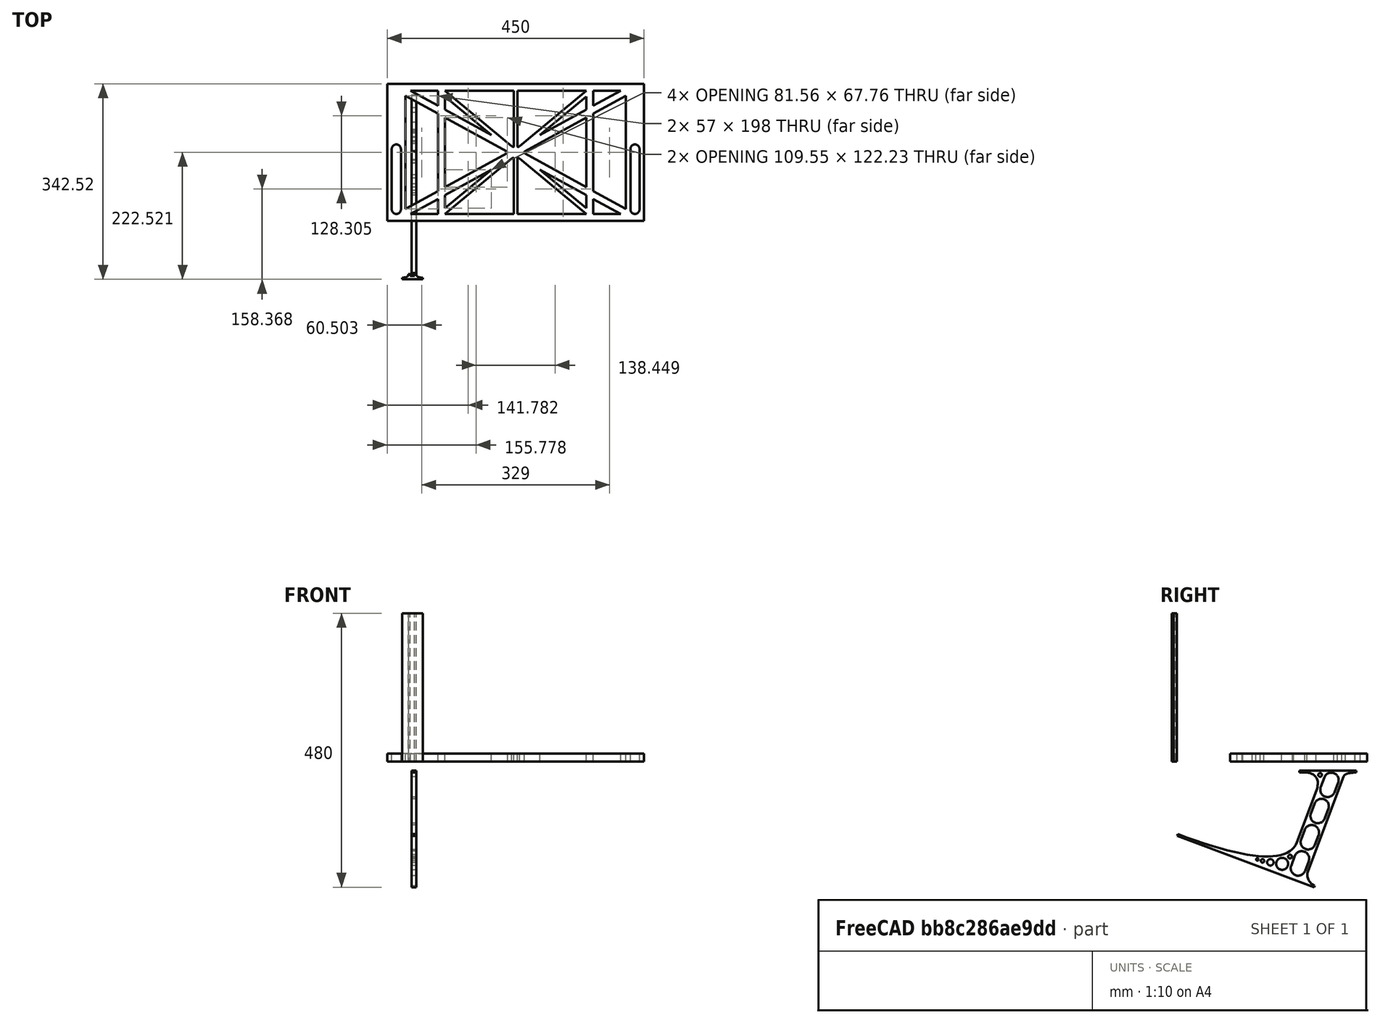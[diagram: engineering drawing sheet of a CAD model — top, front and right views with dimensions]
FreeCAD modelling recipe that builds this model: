
FCSTD DOCUMENT  (FreeCAD 0.19R0.19.2)
Label: laptopStand064
License: All rights reserved
LicenseURL: http://en.wikipedia.org/wiki/All_rights_reserved
objects: Sketcher::SketchObject×3, Part::Extrusion×3
note: 6 computed .brp shape members not serialized (recipe doc carries the construction recipe); baked Part::Feature solids carry a one-line shape summary decoded from their .brp

FEATURE [Sketcher::SketchObject] Sketch
  FullyConstrained = false
  sketch-geometry (101):
    g0: LineSegment StartX=-10.9272 StartY=-82.7794 StartZ=0 EndX=46.0728 EndY=-51.4823 EndZ=0
    g1: LineSegment StartX=366.073 StartY=-91.7794 StartZ=0 EndX=318.073 EndY=-65.424 EndZ=0
    g2: LineSegment StartX=-10.9272 StartY=77.3346 StartZ=0 EndX=-10.9272 EndY=-82.7794 EndZ=0
    g3: LineSegment StartX=375.073 StartY=-82.7794 StartZ=0 EndX=375.073 EndY=83.9235 EndZ=0
    g4: LineSegment StartX=-1.92719 StartY=-91.7794 StartZ=0 EndX=46.0728 EndY=-91.7794 EndZ=0
    g5: LineSegment StartX=318.073 StartY=124.221 StartZ=0 EndX=366.073 EndY=124.221 EndZ=0
    g6: LineSegment StartX=306.073 StartY=-81.8102 StartZ=0 EndX=224.513 EndY=-14.0532 EndZ=0
    g7: LineSegment StartX=58.0728 StartY=114.251 StartZ=0 EndX=139.632 EndY=46.4944 EndZ=0
    g8: LineSegment StartX=306.073 StartY=124.221 StartZ=0 EndX=189.124 EndY=27.0628 EndZ=0
    g9: LineSegment StartX=58.0728 StartY=-91.7794 StartZ=0 EndX=175.022 EndY=5.37834 EndZ=0
    g10: LineSegment StartX=58.0728 StartY=-81.8102 StartZ=0 EndX=58.0728 EndY=-58.8351 EndZ=0
    g11: LineSegment StartX=306.073 StartY=114.251 StartZ=0 EndX=306.073 EndY=91.2763 EndZ=0
    g12: LineSegment StartX=224.513 StartY=46.4944 StartZ=0 EndX=306.073 EndY=114.251 EndZ=0
    g13: LineSegment StartX=175.022 StartY=27.0628 StartZ=0 EndX=58.0728 EndY=124.221 EndZ=0
    g14: LineSegment StartX=139.632 StartY=-14.0532 StartZ=0 EndX=58.0728 EndY=-81.8102 EndZ=0
    g15: LineSegment StartX=224.513 StartY=46.4944 StartZ=0 EndX=306.073 EndY=91.2763 EndZ=0
    g16: LineSegment StartX=139.632 StartY=-14.0532 StartZ=0 EndX=58.0728 EndY=-58.8351 EndZ=0
    g17: LineSegment StartX=189.124 StartY=5.37834 StartZ=0 EndX=306.073 EndY=-91.7794 EndZ=0
    g18: LineSegment StartX=306.073 StartY=77.3346 StartZ=0 EndX=306.073 EndY=-44.8935 EndZ=0
    g19: LineSegment StartX=318.073 StartY=83.9235 StartZ=0 EndX=318.073 EndY=-51.4823 EndZ=0
    g20: LineSegment StartX=306.073 StartY=-58.8351 StartZ=0 EndX=224.513 EndY=-14.0532 EndZ=0
    g21: LineSegment StartX=306.073 StartY=-58.8351 StartZ=0 EndX=306.073 EndY=-81.8102 EndZ=0
    g22: LineSegment StartX=318.073 StartY=-51.4823 StartZ=0 EndX=375.073 EndY=-82.7794 EndZ=0
    g23: LineSegment StartX=318.073 StartY=-65.424 StartZ=0 EndX=318.073 EndY=-91.7794 EndZ=0
    g24: LineSegment StartX=318.073 StartY=-91.7794 StartZ=0 EndX=366.073 EndY=-91.7794 EndZ=0
    g25: LineSegment StartX=58.0728 StartY=-44.8935 StartZ=0 EndX=58.0728 EndY=77.3346 EndZ=0
    g26: LineSegment StartX=46.0728 StartY=-65.424 StartZ=0 EndX=-1.92719 EndY=-91.7794 EndZ=0
    g27: LineSegment StartX=46.0728 StartY=-65.424 StartZ=0 EndX=46.0728 EndY=-91.7794 EndZ=0
    g28: LineSegment StartX=58.0728 StartY=91.2763 StartZ=0 EndX=58.0728 EndY=114.251 EndZ=0
    g29: LineSegment StartX=46.0728 StartY=77.3346 StartZ=0 EndX=46.0728 EndY=-51.4823 EndZ=0
    g30: LineSegment StartX=58.0728 StartY=91.2763 StartZ=0 EndX=139.632 EndY=46.4944 EndZ=0
    g31: LineSegment StartX=-42.9272 StartY=136.221 StartZ=0 EndX=-42.9272 EndY=-103.779 EndZ=0
    g32: LineSegment StartX=407.073 StartY=136.221 StartZ=0 EndX=407.073 EndY=-103.779 EndZ=0
    g33: LineSegment StartX=179.022 StartY=27.0628 StartZ=0 EndX=179.022 EndY=124.221 EndZ=0
    g34: LineSegment StartX=185.124 StartY=27.0628 StartZ=0 EndX=185.124 EndY=124.221 EndZ=0
    g35: ArcOfCircle CenterX=-26.9272 CenterY=22.1087 CenterZ=0 NormalX=0 NormalY=0 NormalZ=1 AngleXU=0 Radius=8 StartAngle=1e-16 EndAngle=3.14159
    g36: ArcOfCircle CenterX=-26.9272 CenterY=-83.7794 CenterZ=0 NormalX=0 NormalY=0 NormalZ=1 AngleXU=0 Radius=8 StartAngle=3.14159 EndAngle=6.28319
    g37: LineSegment StartX=-34.9272 StartY=22.1087 StartZ=0 EndX=-34.9272 EndY=-83.7794 EndZ=0
    g38: LineSegment StartX=-18.9272 StartY=22.1087 StartZ=0 EndX=-18.9272 EndY=-83.7794 EndZ=0
    g39: LineSegment StartX=185.124 StartY=-91.7794 StartZ=0 EndX=306.073 EndY=-91.7794 EndZ=0
    g40: LineSegment StartX=179.022 StartY=-91.7794 StartZ=0 EndX=58.0728 EndY=-91.7794 EndZ=0
    g41: LineSegment StartX=306.073 StartY=124.221 StartZ=0 EndX=185.124 EndY=124.221 EndZ=0
    g42: LineSegment StartX=179.022 StartY=124.221 StartZ=0 EndX=58.0728 EndY=124.221 EndZ=0
    g43: ArcOfCircle CenterX=391.073 CenterY=22.1087 CenterZ=0 NormalX=0 NormalY=0 NormalZ=1 AngleXU=0 Radius=8 StartAngle=-4.4e-15 EndAngle=3.14159
    g44: LineSegment StartX=399.073 StartY=22.1087 StartZ=0 EndX=399.073 EndY=-83.7794 EndZ=0
    g45: LineSegment StartX=383.073 StartY=22.1087 StartZ=0 EndX=383.073 EndY=-83.7794 EndZ=0
    g46: ArcOfCircle CenterX=391.073 CenterY=-83.7794 CenterZ=0 NormalX=0 NormalY=0 NormalZ=1 AngleXU=0 Radius=8 StartAngle=3.14159 EndAngle=6.28319
    g47: Circle CenterX=175.022 CenterY=27.0628 CenterZ=0 NormalX=0 NormalY=0 NormalZ=1 AngleXU=0 Radius=1
    g48: Circle CenterX=179.022 CenterY=24.8665 CenterZ=0 NormalX=0 NormalY=0 NormalZ=1 AngleXU=0 Radius=1
    g49: Circle CenterX=179.022 CenterY=27.0628 CenterZ=0 NormalX=0 NormalY=0 NormalZ=1 AngleXU=0 Radius=1
    g50: BSplineCurve PolesCount=3 KnotsCount=2 Degree=2 IsPeriodic=0
    g51: GeomPoint X=175.022 Y=27.0628 Z=0
    g52: GeomPoint X=179.022 Y=27.0628 Z=0
    g53: Circle CenterX=189.124 CenterY=27.0628 CenterZ=0 NormalX=0 NormalY=0 NormalZ=1 AngleXU=0 Radius=1
    g54: Circle CenterX=185.124 CenterY=24.8665 CenterZ=0 NormalX=0 NormalY=0 NormalZ=1 AngleXU=0 Radius=1
    g55: Circle CenterX=185.124 CenterY=27.0628 CenterZ=0 NormalX=0 NormalY=0 NormalZ=1 AngleXU=0 Radius=1
    g56: BSplineCurve PolesCount=3 KnotsCount=2 Degree=2 IsPeriodic=0
    g57: GeomPoint X=189.124 Y=27.0628 Z=0
    g58: GeomPoint X=185.124 Y=27.0628 Z=0
    g59: Circle CenterX=175.022 CenterY=5.37834 CenterZ=0 NormalX=0 NormalY=0 NormalZ=1 AngleXU=0 Radius=1
    g60: Circle CenterX=179.022 CenterY=7.57463 CenterZ=0 NormalX=0 NormalY=0 NormalZ=1 AngleXU=0 Radius=1
    g61: Circle CenterX=179.022 CenterY=5.34704 CenterZ=0 NormalX=0 NormalY=0 NormalZ=1 AngleXU=0 Radius=1
    g62: BSplineCurve PolesCount=3 KnotsCount=2 Degree=2 IsPeriodic=0
    g63: GeomPoint X=175.022 Y=5.37834 Z=0
    g64: GeomPoint X=179.022 Y=5.34704 Z=0
    g65: Circle CenterX=189.124 CenterY=5.37834 CenterZ=0 NormalX=0 NormalY=0 NormalZ=1 AngleXU=0 Radius=1
    g66: Circle CenterX=185.124 CenterY=7.57463 CenterZ=0 NormalX=0 NormalY=0 NormalZ=1 AngleXU=0 Radius=1
    g67: Circle CenterX=185.124 CenterY=5.34704 CenterZ=0 NormalX=0 NormalY=0 NormalZ=1 AngleXU=0 Radius=1
    g68: BSplineCurve PolesCount=3 KnotsCount=2 Degree=2 IsPeriodic=0
    g69: GeomPoint X=189.124 Y=5.37834 Z=0
    g70: GeomPoint X=185.124 Y=5.34704 Z=0
    g71: LineSegment StartX=179.022 StartY=5.34704 StartZ=0 EndX=179.022 EndY=-91.7794 EndZ=0
    g72: LineSegment StartX=185.124 StartY=-91.7794 StartZ=0 EndX=185.124 EndY=5.34704 EndZ=0
    g73: Circle CenterX=165.871 CenterY=18.1458 CenterZ=0 NormalX=0 NormalY=0 NormalZ=1 AngleXU=0 Radius=1
    g74: Circle CenterX=169.377 CenterY=16.2206 CenterZ=0 NormalX=0 NormalY=0 NormalZ=1 AngleXU=0 Radius=1
    g75: Circle CenterX=165.871 CenterY=14.2954 CenterZ=0 NormalX=0 NormalY=0 NormalZ=1 AngleXU=0 Radius=1
    g76: BSplineCurve PolesCount=3 KnotsCount=2 Degree=2 IsPeriodic=0
    g77: GeomPoint X=165.871 Y=18.1458 Z=0
    g78: GeomPoint X=165.871 Y=14.2954 Z=0
    g79: Circle CenterX=198.275 CenterY=18.1458 CenterZ=0 NormalX=0 NormalY=0 NormalZ=1 AngleXU=0 Radius=1
    g80: Circle CenterX=194.768 CenterY=16.2206 CenterZ=0 NormalX=0 NormalY=0 NormalZ=1 AngleXU=0 Radius=1
    g81: Circle CenterX=198.275 CenterY=14.2954 CenterZ=0 NormalX=0 NormalY=0 NormalZ=1 AngleXU=0 Radius=1
    g82: BSplineCurve PolesCount=3 KnotsCount=2 Degree=2 IsPeriodic=0
    g83: GeomPoint X=198.275 Y=18.1458 Z=0
    g84: GeomPoint X=198.275 Y=14.2954 Z=0
    g85: LineSegment StartX=165.871 StartY=18.1458 StartZ=0 EndX=58.0728 EndY=77.3346 EndZ=0
    g86: LineSegment StartX=58.0728 StartY=-44.8935 StartZ=0 EndX=165.871 EndY=14.2954 EndZ=0
    g87: LineSegment StartX=198.275 StartY=18.1458 StartZ=0 EndX=306.073 EndY=77.3346 EndZ=0
    g88: LineSegment StartX=198.275 StartY=14.2954 StartZ=0 EndX=306.073 EndY=-44.8935 EndZ=0
    g89: LineSegment StartX=407.073 StartY=-103.779 StartZ=0 EndX=-42.9272 EndY=-103.779 EndZ=0
    g90: LineSegment StartX=407.073 StartY=136.221 StartZ=0 EndX=-42.9272 EndY=136.221 EndZ=0
    g91: LineSegment StartX=-26.9272 StartY=136.221 StartZ=0 EndX=-26.9272 EndY=98.2206 EndZ=0
    g92: LineSegment StartX=46.0728 StartY=77.3346 StartZ=0 EndX=-10.9272 EndY=77.3346 EndZ=0
    g93: LineSegment StartX=46.0728 StartY=105.865 StartZ=0 EndX=31.5028 EndY=105.865 EndZ=0
    g94: LineSegment StartX=46.0728 StartY=124.221 StartZ=0 EndX=46.0728 EndY=105.865 EndZ=0
    g95: LineSegment StartX=-1.92719 StartY=124.221 StartZ=0 EndX=31.5028 EndY=105.865 EndZ=0
    g96: LineSegment StartX=46.0728 StartY=124.221 StartZ=0 EndX=-1.92719 EndY=124.221 EndZ=0
    g97: LineSegment StartX=318.073 StartY=83.9235 StartZ=0 EndX=375.073 EndY=83.9235 EndZ=0
    g98: LineSegment StartX=318.073 StartY=105.865 StartZ=0 EndX=332.643 EndY=105.865 EndZ=0
    g99: LineSegment StartX=332.643 StartY=105.865 StartZ=0 EndX=366.073 EndY=124.221 EndZ=0
    g100: LineSegment StartX=318.073 StartY=124.221 StartZ=0 EndX=318.073 EndY=105.865 EndZ=0
  constraints (192):
    c: Horizontal(g4)
    c: Horizontal(g5)
    c: Coincident(g30,g7)
    c: Coincident(g12,g15)
    c: Coincident(g16,g14)
    c: Coincident(g20,g6)
    c: Coincident(g12,g11)
    c: Tangent(g11,g18)
    c: Coincident(g15,g11)
    c: Coincident(g21,g6)
    c: Tangent(g1,g20)
    c: Tangent(g18,g21)
    c: Coincident(g19,g22)
    c: Coincident(g23,g1)
    c: Tangent(g19,g23)
    c: Coincident(g14,g10)
    c: Tangent(g10,g25)
    c: Coincident(g16,g10)
    c: Tangent(g16,g26)
    c: Coincident(g27,g26)
    c: Coincident(g0,g29)
    c: Tangent(g25,g28)
    c: Coincident(g7,g28)
    c: Coincident(g30,g28)
    c: Block(g13)
    c: Block(g8)
    c: Block(g22)
    c: Block(g3)
    c: Block(g20)
    c: Block(g21)
    c: Block(g1)
    c: Block(g23)
    c: Block(g12)
    c: Block(g17)
    c: Block(g9)
    c: Block(g16)
    c: Block(g14)
    c: Block(g27)
    c: Block(g26)
    c: Block(g0)
    c: Block(g2)
    c: Block(g7)
    c: Block(g28)
    c: Block(g18)
    c: Block(g5)
    c: Block(g24)
    c: Block(g4)
    c: Vertical(g31)
    c: Vertical(g32)
    c: Block(g32)
    c: Block(g31)
    c: Vertical(g33)
    c: Vertical(g34)
    c: Block(g33)
    c: Block(g34)
    c: Tangent(g35,g38) = 1.5708
    c: Tangent(g35,g37) = -1.5708
    c: Tangent(g37,g36) = -1.5708
    c: Tangent(g38,g36) = 1.5708
    c: Vertical(g37)
    c: Equal(g35,g36)
    c: Block(g38)
    c: Block(g37)
    c: Coincident(g39,g17)
    c: Horizontal(g39)
    c: Coincident(g40,g9)
    c: Horizontal(g40)
    c: Coincident(g41,g8)
    c: Coincident(g41,g34)
    c: Horizontal(g41)
    c: Coincident(g42,g33)
    c: Coincident(g42,g13)
    c: Horizontal(g42)
    c: Tangent(g43,g44) = 1.5708
    c: Tangent(g44,g46) = 1.5708
    c: Equal(g43,g46)
    c: Coincident(g45,g43)
    c: Coincident(g45,g46)
    c: Block(g44)
    c: Block(g45)
    c: Coincident(g50,g13)
    c: Weight(g47) = 1
    c: Equal(g47,g48)
    c: Equal(g47,g49)
    c: Coincident(g50,g33)
    c: InternalAlignment(g47,g50)
    c: InternalAlignment(g48,g50)
    c: InternalAlignment(g49,g50)
    c: InternalAlignment(g51,g50)
    c: InternalAlignment(g52,g50)
    c: Coincident(g56,g8)
    c: Weight(g53) = 1
    c: Equal(g53,g54)
    c: Equal(g53,g55)
    c: Coincident(g56,g34)
    c: InternalAlignment(g53,g56)
    c: InternalAlignment(g54,g56)
    c: InternalAlignment(g55,g56)
    c: InternalAlignment(g57,g56)
    c: InternalAlignment(g58,g56)
    c: Block(g56)
    c: Block(g50)
    c: Coincident(g62,g9)
    c: Weight(g59) = 1
    c: Equal(g59,g60)
    c: Equal(g59,g61)
    c: InternalAlignment(g59,g62)
    c: InternalAlignment(g60,g62)
    c: InternalAlignment(g61,g62)
    c: InternalAlignment(g63,g62)
    c: InternalAlignment(g64,g62)
    c: Weight(g65) = 1
    c: Equal(g65,g66)
    c: Equal(g65,g67)
    c: InternalAlignment(g65,g68)
    c: InternalAlignment(g66,g68)
    c: InternalAlignment(g67,g68)
    c: InternalAlignment(g69,g68)
    c: InternalAlignment(g70,g68)
    c: Block(g68)
    c: Block(g62)
    c: Coincident(g71,g62)
    c: Coincident(g71,g40)
    c: Vertical(g71)
    c: Coincident(g72,g39)
    c: Coincident(g72,g68)
    c: Vertical(g72)
    c: Weight(g73) = 1
    c: Equal(g73,g74)
    c: Equal(g73,g75)
    c: InternalAlignment(g73,g76)
    c: InternalAlignment(g74,g76)
    c: InternalAlignment(g75,g76)
    c: InternalAlignment(g77,g76)
    c: InternalAlignment(g78,g76)
    c: Weight(g79) = 1
    c: Equal(g79,g80)
    c: Equal(g79,g81)
    c: InternalAlignment(g79,g82)
    c: InternalAlignment(g80,g82)
    c: InternalAlignment(g81,g82)
    c: InternalAlignment(g83,g82)
    c: InternalAlignment(g84,g82)
    c: Block(g76)
    c: Block(g82)
    c: Coincident(g85,g76)
    c: Coincident(g85,g25)
    c: Coincident(g86,g25)
    c: Coincident(g86,g76)
    c: Coincident(g87,g82)
    c: Coincident(g87,g18)
    c: Coincident(g88,g82)
    c: Coincident(g88,g18)
    c: Block(g25)
    c: Coincident(g89,g32)
    c: Coincident(g89,g31)
    c: Horizontal(g89)
    c: Distance(g89) = 450
    c: Coincident(g90,g32)
    c: Coincident(g90,g31)
    c: Horizontal(g90)
    c: PointOnObject(g91,g90)
    c: Vertical(g91)
    c: Distance(g91) = 38
    c: Horizontal(g92)
    c: Coincident(g29,g92)
    c: Horizontal(g93)
    c: Vertical(g94)
    c: Block(g94)
    c: Block(g93)
    c: Block(g92)
    c: Distance(g94) = 18.3554
    c: Coincident(g96,g94)
    c: Coincident(g96,g95)
    c: Horizontal(g96)
    c: Block(g96)
    c: Block(g95)
    c: Coincident(g93,g95)
    c: Coincident(g2,g92)
    c: Coincident(g97,g19)
    c: Horizontal(g97)
    c: Horizontal(g98)
    c: Block(g97)
    c: Block(g11)
    c: Coincident(g99,g5)
    c: Coincident(g100,g5)
    c: Coincident(g100,g98)
    c: Vertical(g100)
    c: Block(g100)
    c: Coincident(g98,g99)
    c: Block(g99)
    c: Coincident(g3,g97)
FEATURE [Sketcher::SketchObject] Sketch001
  FullyConstrained = true
  MapMode = 4
  Placement = pos=(0,0,0) rot=(0.57735,0.57735,0.57735;2.0944rad)
  Support = -> [Sketch]
  sketch-geometry (46):
    g0: BSplineCurve PolesCount=3 KnotsCount=2 Degree=2 IsPeriodic=0
    g1: ArcOfCircle CenterX=73.1223 CenterY=-32.291 CenterZ=0 NormalX=0 NormalY=0 NormalZ=1 AngleXU=0 Radius=13 StartAngle=5.92268 EndAngle=9.06428
    g2: ArcOfCircle CenterX=66.7816 CenterY=-49.1439 CenterZ=0 NormalX=0 NormalY=0 NormalZ=1 AngleXU=0 Radius=13 StartAngle=2.78068 EndAngle=5.92131
    g3: ArcOfCircle CenterX=55.9263 CenterY=-78.1807 CenterZ=0 NormalX=0 NormalY=0 NormalZ=1 AngleXU=0 Radius=13 StartAngle=5.92268 EndAngle=9.06428
    g4: ArcOfCircle CenterX=49.5884 CenterY=-95.0342 CenterZ=0 NormalX=0 NormalY=0 NormalZ=1 AngleXU=0 Radius=13 StartAngle=2.78068 EndAngle=5.92131
    g5: ArcOfCircle CenterX=38.7206 CenterY=-124.067 CenterZ=0 NormalX=0 NormalY=0 NormalZ=1 AngleXU=0 Radius=13 StartAngle=5.92268 EndAngle=9.06428
    g6: ArcOfCircle CenterX=32.3875 CenterY=-140.92 CenterZ=0 NormalX=0 NormalY=0 NormalZ=1 AngleXU=0 Radius=13 StartAngle=2.78068 EndAngle=5.92131
    g7: ArcOfCircle CenterX=21.4715 CenterY=-169.934 CenterZ=0 NormalX=0 NormalY=0 NormalZ=1 AngleXU=0 Radius=13 StartAngle=5.92268 EndAngle=9.06428
    g8: ArcOfCircle CenterX=15.1336 CenterY=-186.787 CenterZ=0 NormalX=0 NormalY=0 NormalZ=1 AngleXU=0 Radius=13 StartAngle=2.78068 EndAngle=5.92131
    g9-g12: Circle x4 (B-spline internal-alignment scaffolding for g13; pole/knot coordinates omitted)
    g13: BSplineCurve PolesCount=4 KnotsCount=2 Degree=3 IsPeriodic=0
    g14: GeomPoint X=28.8094 Y=-19.0875 Z=0
    g15: GeomPoint X=47.0443 Y=-50.4712 Z=0
    g16: Circle CenterX=53.5586 CenterY=-23.2695 CenterZ=0 NormalX=0 NormalY=0 NormalZ=1 AngleXU=0 Radius=3.24518
    g17: Circle CenterX=-195.441 CenterY=-127.082 CenterZ=0 NormalX=0 NormalY=0 NormalZ=1 AngleXU=0 Radius=1
    g18: Circle CenterX=-8.24091 CenterY=-197.481 CenterZ=0 NormalX=0 NormalY=0 NormalZ=1 AngleXU=0 Radius=1
    g19: Circle CenterX=12.8789 CenterY=-141.321 CenterZ=0 NormalX=0 NormalY=0 NormalZ=1 AngleXU=0 Radius=1
    g20: BSplineCurve PolesCount=3 KnotsCount=2 Degree=2 IsPeriodic=0
    g21: GeomPoint X=-195.441 Y=-127.082 Z=0
    g22: GeomPoint X=12.8789 Y=-141.321 Z=0
    g23: Circle CenterX=-12.8016 CenterY=-179.036 CenterZ=0 NormalX=0 NormalY=0 NormalZ=1 AngleXU=0 Radius=10.5072
    g24: Circle CenterX=0.933922 CenterY=-166.43 CenterZ=0 NormalX=0 NormalY=0 NormalZ=1 AngleXU=0 Radius=3.26661
    g25: Circle CenterX=-33.5518 CenterY=-176.44 CenterZ=0 NormalX=0 NormalY=0 NormalZ=1 AngleXU=0 Radius=5.64388
    g26: Circle CenterX=-47.2366 CenterY=-173.859 CenterZ=0 NormalX=0 NormalY=0 NormalZ=1 AngleXU=0 Radius=3.01653
    g27: Circle CenterX=-56.2595 CenterY=-171.456 CenterZ=0 NormalX=0 NormalY=0 NormalZ=1 AngleXU=0 Radius=2.12826
    g28: ArcOfCircle CenterX=51.2151 CenterY=-198.473 CenterZ=0 NormalX=0 NormalY=0 NormalZ=1 AngleXU=0 Radius=20 StartAngle=2.78189 EndAngle=4.35269
    g29: LineSegment StartX=32.4951 StartY=-191.433 StartZ=0 EndX=94.6578 EndY=-26.1352 EndZ=0
    g30: LineSegment StartX=43.1192 StartY=-220.001 StartZ=0 EndX=-196.497 EndY=-129.89 EndZ=0
    g31: LineSegment StartX=43.1192 StartY=-220.001 StartZ=0 EndX=44.1752 EndY=-217.193 EndZ=0
    g32: LineSegment StartX=117.223 StartY=-19.0875 StartZ=0 EndX=117.223 EndY=-16.0875 EndZ=0
    g33: LineSegment StartX=117.223 StartY=-16.0875 StartZ=0 EndX=17.2232 EndY=-16.0875 EndZ=0
    g34: LineSegment StartX=17.2232 StartY=-16.0875 StartZ=0 EndX=17.2232 EndY=-19.0875 EndZ=0
    g35: LineSegment StartX=28.8094 StartY=-19.0875 StartZ=0 EndX=17.2232 EndY=-19.0875 EndZ=0
    g36: LineSegment StartX=47.0443 StartY=-50.4712 StartZ=0 EndX=12.8789 EndY=-141.321 EndZ=0
    g37: LineSegment StartX=-195.441 StartY=-127.082 StartZ=0 EndX=-196.497 EndY=-129.89 EndZ=0
    g38: LineSegment StartX=85.2866 StartY=-36.8766 StartZ=0 EndX=78.9396 EndY=-53.7463 EndZ=0
    g39: LineSegment StartX=60.9579 StartY=-27.7053 StartZ=0 EndX=54.6191 EndY=-44.5532 EndZ=0
    g40: LineSegment StartX=68.0907 StartY=-82.7664 StartZ=0 EndX=61.7465 EndY=-99.6365 EndZ=0
    g41: LineSegment StartX=43.7619 StartY=-73.595 StartZ=0 EndX=37.426 EndY=-90.4435 EndZ=0
    g42: LineSegment StartX=50.885 StartY=-128.652 StartZ=0 EndX=44.5456 EndY=-145.522 EndZ=0
    g43: LineSegment StartX=26.5562 StartY=-119.481 StartZ=0 EndX=20.2251 EndY=-136.329 EndZ=0
    g44: LineSegment StartX=9.3071 StartY=-165.349 StartZ=0 EndX=2.97115 EndY=-182.197 EndZ=0
    g45: LineSegment StartX=33.6358 StartY=-174.52 StartZ=0 EndX=27.2917 EndY=-191.39 EndZ=0
  constraints (71):
    c: Block(g0)
    c: Block(g1)
    c: Block(g2)
    c: Block(g4)
    c: Block(g3)
    c: Block(g6)
    c: Block(g5)
    c: Block(g8)
    c: Block(g7)
    c: Weight(g9) = 1
    c: Equal(g9,g10)
    c: Equal(g9,g11)
    c: Equal(g9,g12)
    c: InternalAlignment(g9-g12 -> g13) x4
    c: InternalAlignment(g14,g13)
    c: InternalAlignment(g15,g13)
    c: Block(g16)
    c: Weight(g17) = 1
    c: Equal(g17,g18)
    c: Equal(g17,g19)
    c: InternalAlignment(g17,g20)
    c: InternalAlignment(g18,g20)
    c: InternalAlignment(g19,g20)
    c: InternalAlignment(g21,g20)
    c: InternalAlignment(g22,g20)
    c: Block(g20)
    c: Block(g23)
    c: Block(g24)
    c: Block(g25)
    c: Block(g26)
    c: Block(g27)
    c: Block(g28)
    c: Coincident(g29,g28)
    c: Coincident(g29,g0)
    c: Block(g13)
    c: Coincident(g31,g30)
    c: Coincident(g31,g28)
    c: Block(g31)
    c: Coincident(g32,g0)
    c: Vertical(g32)
    c: Coincident(g33,g32)
    c: Horizontal(g33)
    c: Coincident(g34,g33)
    c: Vertical(g34)
    c: Block(g33)
    c: Coincident(g35,g13)
    c: Coincident(g35,g34)
    c: Horizontal(g35)
    c: Coincident(g36,g13)
    c: Coincident(g36,g20)
    c: Coincident(g37,g20)
    c: Coincident(g37,g30)
    c: Block(g30)
    c: Coincident(g38,g1)
    c: Coincident(g38,g2)
    c: Coincident(g39,g1)
    c: Coincident(g39,g2)
    c: Coincident(g40,g3)
    c: Coincident(g40,g4)
    c: Coincident(g41,g3)
    c: Coincident(g41,g4)
    c: Coincident(g42,g5)
    c: Coincident(g42,g6)
    c: Coincident(g43,g5)
    c: Coincident(g43,g6)
    c: Coincident(g44,g7)
    c: Coincident(g44,g8)
    c: Coincident(g45,g7)
    c: Coincident(g45,g8)
    c: Distance(g30) = 256
    c: Distance(g33) = 100
FEATURE [Part::Extrusion] Extrude002
  Base = -> Sketch001
  Dir = (1,0,0)
  DirMode = 2
  FaceMakerClass = Part::FaceMakerBullseye
  LengthFwd = 8
  LengthRev = 0
  Solid = true
  Symmetric = false
FEATURE [Sketcher::SketchObject] Sketch002
  FullyConstrained = true
  sketch-geometry (20):
    g0: LineSegment StartX=-2.77179 StartY=-200.304 StartZ=0 EndX=5.22821 EndY=-200.304 EndZ=0
    g1: LineSegment StartX=5.22821 StartY=-200.304 StartZ=0 EndX=5.22821 EndY=-197.304 EndZ=0
    g2: LineSegment StartX=-2.77179 StartY=-200.304 StartZ=0 EndX=-2.77179 EndY=-197.304 EndZ=0
    g3: LineSegment StartX=5.22821 StartY=-197.304 StartZ=0 EndX=8.22821 EndY=-197.304 EndZ=0
    g4: LineSegment StartX=-2.77179 StartY=-197.304 StartZ=0 EndX=-5.77179 EndY=-197.304 EndZ=0
    g5: LineSegment StartX=19.2282 StartY=-203.304 StartZ=0 EndX=19.2282 EndY=-206.304 EndZ=0
    g6: LineSegment StartX=-16.7718 StartY=-203.304 StartZ=0 EndX=-16.7718 EndY=-206.304 EndZ=0
    g7: LineSegment StartX=-16.7718 StartY=-206.304 StartZ=0 EndX=19.2282 EndY=-206.304 EndZ=0
    g8: Circle CenterX=-16.7718 CenterY=-203.304 CenterZ=0 NormalX=0 NormalY=0 NormalZ=1 AngleXU=0 Radius=1
    g9: Circle CenterX=-5.77179 CenterY=-203.304 CenterZ=0 NormalX=0 NormalY=0 NormalZ=1 AngleXU=0 Radius=1
    g10: Circle CenterX=-5.77179 CenterY=-197.304 CenterZ=0 NormalX=0 NormalY=0 NormalZ=1 AngleXU=0 Radius=1
    g11: BSplineCurve PolesCount=3 KnotsCount=2 Degree=2 IsPeriodic=0
    g12: GeomPoint X=-16.7718 Y=-203.304 Z=0
    g13: GeomPoint X=-5.77179 Y=-197.304 Z=0
    g14: Circle CenterX=19.2282 CenterY=-203.304 CenterZ=0 NormalX=0 NormalY=0 NormalZ=1 AngleXU=0 Radius=1
    g15: Circle CenterX=8.22821 CenterY=-203.304 CenterZ=0 NormalX=0 NormalY=0 NormalZ=1 AngleXU=0 Radius=1
    g16: Circle CenterX=8.22821 CenterY=-197.304 CenterZ=0 NormalX=0 NormalY=0 NormalZ=1 AngleXU=0 Radius=1
    g17: BSplineCurve PolesCount=3 KnotsCount=2 Degree=2 IsPeriodic=0
    g18: GeomPoint X=19.2282 Y=-203.304 Z=0
    g19: GeomPoint X=8.22821 Y=-197.304 Z=0
  constraints (41):
    c: Horizontal(g0)
    c: Distance(g0) = 8
    c: Coincident(g1,g0)
    c: Vertical(g1)
    c: Distance(g1) = 3
    c: Coincident(g2,g0)
    c: Vertical(g2)
    c: Distance(g2) = 3
    c: Coincident(g3,g1)
    c: Horizontal(g3)
    c: Distance(g3) = 3
    c: Coincident(g4,g2)
    c: Horizontal(g4)
    c: Distance(g4) = 3
    c: Vertical(g5)
    c: Vertical(g6)
    c: Coincident(g7,g6)
    c: Coincident(g7,g5)
    c: Weight(g8) = 1
    c: Equal(g8,g9)
    c: Equal(g8,g10)
    c: Coincident(g11,g4)
    c: InternalAlignment(g8,g11)
    c: InternalAlignment(g9,g11)
    c: InternalAlignment(g10,g11)
    c: InternalAlignment(g12,g11)
    c: InternalAlignment(g13,g11)
    c: Coincident(g17,g5)
    c: Weight(g14) = 1
    c: Equal(g14,g15)
    c: Equal(g14,g16)
    c: Coincident(g17,g3)
    c: InternalAlignment(g14,g17)
    c: InternalAlignment(g15,g17)
    c: InternalAlignment(g16,g17)
    c: InternalAlignment(g18,g17)
    c: InternalAlignment(g19,g17)
    c: Block(g7)
    c: Block(g17)
    c: Block(g11)
    c: Block(g6)
FEATURE [Part::Extrusion] Extrude003
  Base = -> Sketch002
  Dir = (0,0,1)
  DirMode = 2
  FaceMakerClass = Part::FaceMakerBullseye
  LengthFwd = 260
  LengthRev = 0
  Solid = true
  Symmetric = false
FEATURE [Part::Extrusion] Extrude
  Base = -> Sketch
  Dir = (0,0,1)
  DirMode = 2
  FaceMakerClass = Part::FaceMakerBullseye
  LengthFwd = 14
  LengthRev = 0
  Solid = true
  Symmetric = false
